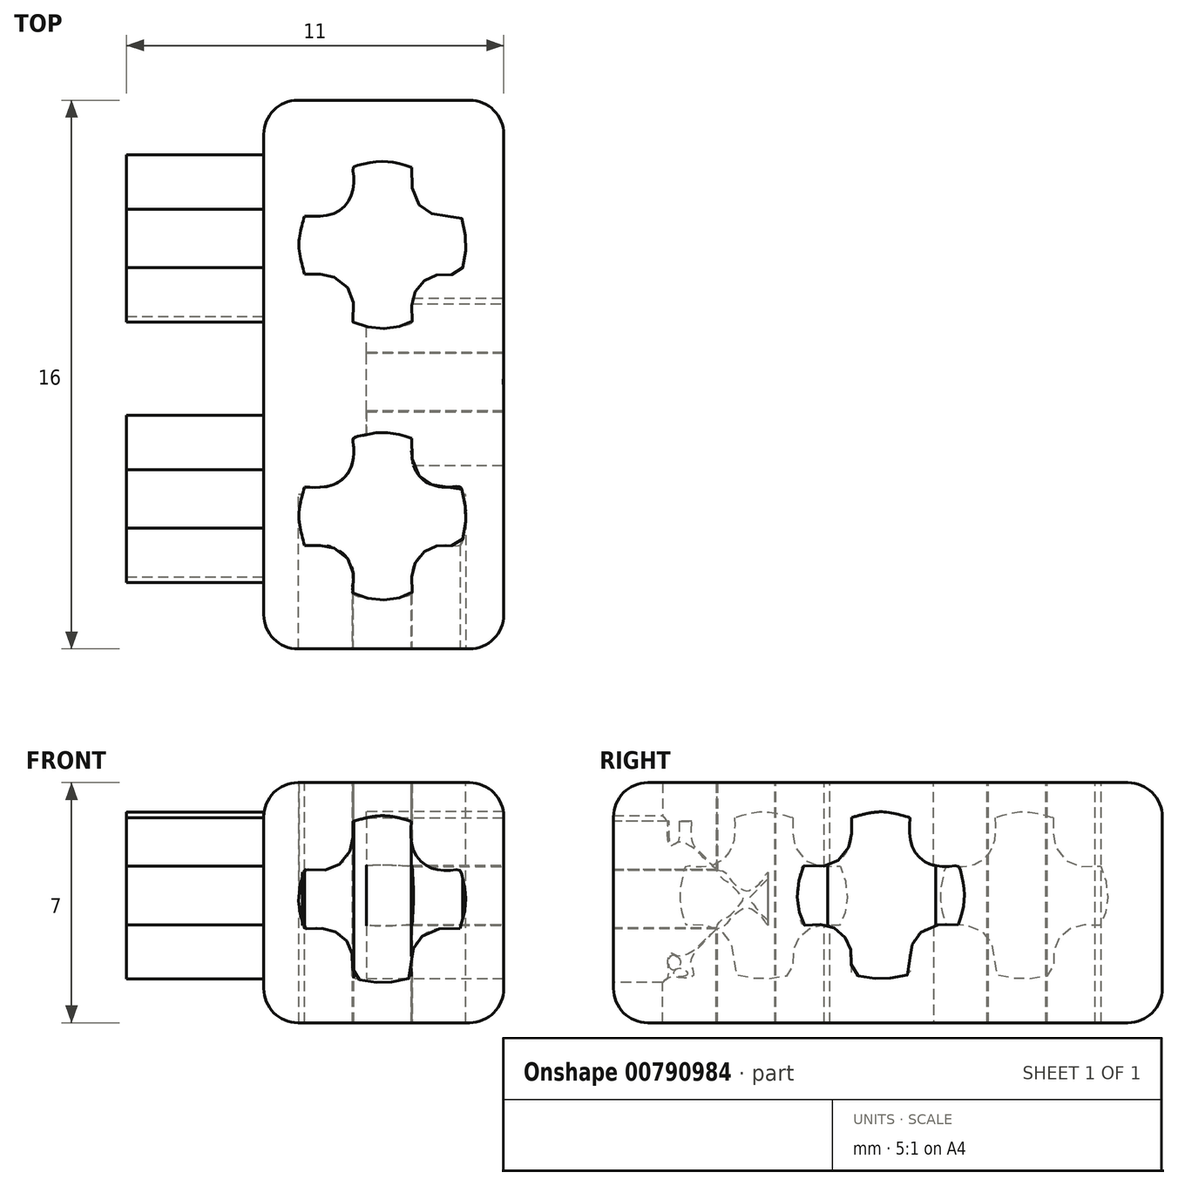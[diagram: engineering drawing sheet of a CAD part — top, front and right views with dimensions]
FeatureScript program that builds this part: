
annotation { "Feature Type Name" : "Feature", "Feature Type Description" : "" }
export const myFeature = defineFeature(function(context is Context, id is Id, definition is map)
    precondition{}
    {
        {
            var Q0;
            Q0=qCreatedBy(makeId("Top.planeOp"),FACE);
            var sketch = newSketch(context, id + "F0", { "sketchPlane" : qUnion([Q0])});
            skLineSegment(sketch, "E0.bottom", {"start": v(-3.5, 8) * mm, "end": v(3.5, 8) * mm});
            skLineSegment(sketch, "E0.top", {"start": v(-3.5, -8) * mm, "end": v(3.5, -8) * mm});
            skLineSegment(sketch, "E0.left", {"start": v(-3.5, 8) * mm, "end": v(-3.5, -8) * mm});
            skLineSegment(sketch, "E0.right", {"start": v(3.5, 8) * mm, "end": v(3.5, -8) * mm});
            skPoint(sketch, "E1", {"position": v(0, 8) * mm});
            skPoint(sketch, "E2", {"position": v(-3.5, 0) * mm});
            skSolve(sketch);
        }
        {
            var Q0;
            Q0=makeQuery(id+"F0.imprint","IMPRINT",FACE,{"disambiguationData":[TD([[makeQuery(id+"F0.imprint","IMPRINT",EDGE,{"derivedFrom":sQuery(id+"F0.wireOp",EDGE,"E0.bottom")}),-1.0]])]});
            extrude(context, id + "F1", {"entities" : qUnion([Q0]), "depth" : 7 * mm, "offsetDistance" : 25 * mm});
        }
        {
            var Q0;
            Q0=makeQuery(id+"F1.opExtrude","SWEPT_FACE",FACE,{"disambiguationData":[OSD([sQuery(id+"F0.wireOp",EDGE,"E0.left")])]});
            var sketch = newSketch(context, id + "F2", { "sketchPlane" : qUnion([Q0])});
            skFitSpline(sketch, "E3", {"points": [v(-4.82, 5.97) * mm, v(-3.94, 6.14) * mm, v(-3.12, 5.97) * mm], "startDerivative": vector(1.75, 0.5) * mm, "endDerivative": vector(1.65, -0.5) * mm});
            skFitSpline(sketch, "E4", {"points": [v(-3.12, 5.97) * mm, v(-3.12, 5.4) * mm, v(-2.97, 4.97) * mm, v(-2.66, 4.67) * mm, v(-2.31, 4.56) * mm, v(-1.9, 4.55) * mm, v(-1.7, 4.55) * mm, v(-1.62, 4.3) * mm, v(-1.54, 3.92) * mm, v(-1.53, 3.58) * mm, v(-1.58, 3.26) * mm, v(-1.7, 2.85) * mm], "startDerivative": vector(-0.26, -5.18) * mm, "endDerivative": vector(-1.41, -4.37) * mm});
            skFitSpline(sketch, "E5", {"points": [v(-4.82, 5.97) * mm, v(-4.82, 5.68) * mm, v(-4.82, 5.43) * mm, v(-4.85, 5.24) * mm, v(-5.02, 4.9) * mm, v(-5.22, 4.72) * mm, v(-5.48, 4.6) * mm, v(-5.8, 4.55) * mm, v(-6.24, 4.55) * mm, v(-6.33, 4.27) * mm, v(-6.39, 3.98) * mm, v(-6.4, 3.66) * mm, v(-6.38, 3.37) * mm, v(-6.32, 3.1) * mm, v(-6.24, 2.85) * mm, v(-6.05, 2.85) * mm, v(-5.73, 2.85) * mm, v(-5.48, 2.81) * mm, v(-5.3, 2.73) * mm, v(-5.07, 2.56) * mm, v(-4.96, 2.42) * mm, v(-4.88, 2.24) * mm, v(-4.82, 2) * mm, v(-4.82, 1.75) * mm, v(-4.82, 1.43) * mm, v(-4.56, 1.35) * mm, v(-4.21, 1.29) * mm, v(-3.94, 1.28) * mm, v(-3.67, 1.3) * mm, v(-3.3, 1.37) * mm, v(-3.12, 1.43) * mm, v(-3.12, 1.75) * mm, v(-3.11, 2.03) * mm, v(-3.01, 2.35) * mm, v(-2.88, 2.55) * mm, v(-2.61, 2.75) * mm, v(-2.2, 2.85) * mm, v(-1.7, 2.85) * mm], "startDerivative": vector(-0.02, -10.87) * mm, "endDerivative": vector(14.17, -0.52) * mm});
            skFitSpline(sketch, "E6", {"points": [v(2.78, 5.97) * mm, v(3.66, 6.14) * mm, v(4.48, 5.97) * mm], "startDerivative": vector(1.75, 0.5) * mm, "endDerivative": vector(1.65, -0.5) * mm});
            skFitSpline(sketch, "E7", {"points": [v(4.48, 5.97) * mm, v(4.48, 5.4) * mm, v(4.62, 4.97) * mm, v(4.94, 4.67) * mm, v(5.28, 4.56) * mm, v(5.7, 4.55) * mm, v(5.9, 4.55) * mm, v(5.98, 4.3) * mm, v(6.05, 3.92) * mm, v(6.06, 3.58) * mm, v(6.02, 3.26) * mm, v(5.9, 2.85) * mm], "startDerivative": vector(-0.26, -5.18) * mm, "endDerivative": vector(-1.41, -4.37) * mm});
            skFitSpline(sketch, "E8", {"points": [v(2.78, 5.97) * mm, v(2.78, 5.68) * mm, v(2.77, 5.43) * mm, v(2.75, 5.24) * mm, v(2.57, 4.9) * mm, v(2.38, 4.72) * mm, v(2.12, 4.6) * mm, v(1.8, 4.55) * mm, v(1.35, 4.55) * mm, v(1.27, 4.27) * mm, v(1.2, 3.98) * mm, v(1.19, 3.66) * mm, v(1.22, 3.37) * mm, v(1.27, 3.1) * mm, v(1.35, 2.85) * mm, v(1.55, 2.85) * mm, v(1.86, 2.85) * mm, v(2.11, 2.81) * mm, v(2.3, 2.73) * mm, v(2.52, 2.56) * mm, v(2.63, 2.42) * mm, v(2.72, 2.24) * mm, v(2.77, 2) * mm, v(2.78, 1.75) * mm, v(2.78, 1.43) * mm, v(3.03, 1.35) * mm, v(3.38, 1.29) * mm, v(3.66, 1.28) * mm, v(3.93, 1.3) * mm, v(4.3, 1.37) * mm, v(4.48, 1.43) * mm, v(4.48, 1.75) * mm, v(4.48, 2.03) * mm, v(4.58, 2.35) * mm, v(4.72, 2.55) * mm, v(4.99, 2.75) * mm, v(5.4, 2.85) * mm, v(5.9, 2.85) * mm], "startDerivative": vector(-0.02, -10.87) * mm, "endDerivative": vector(14.17, -0.52) * mm});
            skSolve(sketch);
        }
        {
            var Q0;
            Q0=makeQuery(id+"F2.imprint","IMPRINT",FACE,{"disambiguationData":[TD([[makeQuery(id+"F2.imprint","IMPRINT",EDGE,{"derivedFrom":sQuery(id+"F2.wireOp",EDGE,"E3")}),-1.0]])]});
            var Q1;
            Q1=makeQuery(id+"F2.imprint","IMPRINT",FACE,{"disambiguationData":[TD([[makeQuery(id+"F2.imprint","IMPRINT",EDGE,{"derivedFrom":sQuery(id+"F2.wireOp",EDGE,"d630b020-bbd6-4e47-9868-e03ddda9818e")}),-1.0]])]});
            var Q2;
            Q2=makeQuery(id+"F2.imprint","IMPRINT",FACE,{"disambiguationData":[TD([[makeQuery(id+"F2.imprint","IMPRINT",EDGE,{"derivedFrom":sQuery(id+"F2.wireOp",EDGE,"E6")}),-1.0]])]});
            extrude(context, id + "F3", {"entities" : qUnion([Q0, Q1, Q2]), "depth" : 4 * mm, "offsetDistance" : 25 * mm});
        }
        {
            var Q0;
            Q0=makeQuery(id+"F1.opExtrude","SWEPT_FACE",FACE,{"disambiguationData":[OSD([sQuery(id+"F0.wireOp",EDGE,"E0.top")])]});
            var sketch = newSketch(context, id + "F4", { "sketchPlane" : qUnion([Q0])});
            skFitSpline(sketch, "E9", {"points": [v(-0.9, 5.87) * mm, v(-0.02, 6.04) * mm, v(0.8, 5.87) * mm], "startDerivative": vector(1.75, 0.5) * mm, "endDerivative": vector(1.65, -0.5) * mm});
            skFitSpline(sketch, "E10", {"points": [v(0.8, 5.87) * mm, v(0.8, 5.3) * mm, v(0.95, 4.87) * mm, v(1.26, 4.57) * mm, v(1.6, 4.46) * mm, v(2.02, 4.45) * mm, v(2.22, 4.45) * mm, v(2.3, 4.2) * mm, v(2.38, 3.82) * mm, v(2.39, 3.48) * mm, v(2.34, 3.16) * mm, v(2.22, 2.75) * mm], "startDerivative": vector(-0.26, -5.18) * mm, "endDerivative": vector(-1.41, -4.37) * mm});
            skFitSpline(sketch, "E11", {"points": [v(-0.9, 5.87) * mm, v(-0.9, 5.58) * mm, v(-0.9, 5.33) * mm, v(-0.93, 5.14) * mm, v(-1.1, 4.8) * mm, v(-1.3, 4.61) * mm, v(-1.56, 4.49) * mm, v(-1.88, 4.45) * mm, v(-2.32, 4.45) * mm, v(-2.41, 4.17) * mm, v(-2.47, 3.88) * mm, v(-2.49, 3.55) * mm, v(-2.46, 3.27) * mm, v(-2.4, 3) * mm, v(-2.32, 2.75) * mm, v(-2.13, 2.75) * mm, v(-1.81, 2.75) * mm, v(-1.56, 2.71) * mm, v(-1.37, 2.63) * mm, v(-1.15, 2.46) * mm, v(-1.04, 2.32) * mm, v(-0.96, 2.14) * mm, v(-0.9, 1.9) * mm, v(-0.9, 1.65) * mm, v(-0.9, 1.33) * mm, v(-0.64, 1.25) * mm, v(-0.3, 1.19) * mm, v(-0.02, 1.18) * mm, v(0.25, 1.2) * mm, v(0.62, 1.27) * mm, v(0.8, 1.33) * mm, v(0.8, 1.65) * mm, v(0.8, 1.92) * mm, v(0.9, 2.25) * mm, v(1.04, 2.45) * mm, v(1.3, 2.65) * mm, v(1.72, 2.75) * mm, v(2.22, 2.75) * mm], "startDerivative": vector(-0.02, -10.87) * mm, "endDerivative": vector(14.17, -0.52) * mm});
            skFitSpline(sketch, "E12", {"points": [v(9.4, 6.1) * mm, v(10.29, 6.27) * mm, v(11.1, 6.1) * mm], "startDerivative": vector(1.75, 0.5) * mm, "endDerivative": vector(1.65, -0.5) * mm});
            skFitSpline(sketch, "E13", {"points": [v(11.1, 6.1) * mm, v(11.1, 5.54) * mm, v(11.25, 5.1) * mm, v(11.57, 4.8) * mm, v(11.9, 4.7) * mm, v(12.32, 4.68) * mm, v(12.52, 4.68) * mm, v(12.6, 4.44) * mm, v(12.68, 4.05) * mm, v(12.69, 3.71) * mm, v(12.65, 3.4) * mm, v(12.52, 2.98) * mm], "startDerivative": vector(-0.26, -5.18) * mm, "endDerivative": vector(-1.41, -4.37) * mm});
            skFitSpline(sketch, "E14", {"points": [v(9.4, 6.1) * mm, v(9.4, 5.8) * mm, v(9.4, 5.56) * mm, v(9.37, 5.37) * mm, v(9.2, 5.03) * mm, v(9, 4.85) * mm, v(8.74, 4.72) * mm, v(8.42, 4.68) * mm, v(7.98, 4.68) * mm, v(7.9, 4.4) * mm, v(7.83, 4.12) * mm, v(7.81, 3.79) * mm, v(7.84, 3.5) * mm, v(7.9, 3.23) * mm, v(7.98, 2.98) * mm, v(8.18, 2.98) * mm, v(8.5, 2.98) * mm, v(8.74, 2.95) * mm, v(8.93, 2.87) * mm, v(9.15, 2.7) * mm, v(9.26, 2.55) * mm, v(9.35, 2.37) * mm, v(9.4, 2.13) * mm, v(9.4, 1.88) * mm, v(9.4, 1.56) * mm, v(9.66, 1.48) * mm, v(10, 1.42) * mm, v(10.29, 1.4) * mm, v(10.55, 1.43) * mm, v(10.92, 1.5) * mm, v(11.1, 1.56) * mm, v(11.1, 1.88) * mm, v(11.1, 2.16) * mm, v(11.2, 2.49) * mm, v(11.34, 2.68) * mm, v(11.61, 2.88) * mm, v(12.03, 2.98) * mm, v(12.52, 2.98) * mm], "startDerivative": vector(-0.02, -10.87) * mm, "endDerivative": vector(14.17, -0.52) * mm});
            skFitSpline(sketch, "E15", {"points": [v(18.93, 6.02) * mm, v(19.82, 6.2) * mm, v(20.63, 6.02) * mm], "startDerivative": vector(1.75, 0.5) * mm, "endDerivative": vector(1.65, -0.5) * mm});
            skFitSpline(sketch, "E16", {"points": [v(20.63, 6.02) * mm, v(20.64, 5.46) * mm, v(20.78, 5.03) * mm, v(21.1, 4.73) * mm, v(21.44, 4.61) * mm, v(21.85, 4.6) * mm, v(22.05, 4.6) * mm, v(22.13, 4.36) * mm, v(22.2, 3.98) * mm, v(22.22, 3.64) * mm, v(22.18, 3.32) * mm, v(22.05, 2.9) * mm], "startDerivative": vector(-0.26, -5.18) * mm, "endDerivative": vector(-1.41, -4.37) * mm});
            skFitSpline(sketch, "E17", {"points": [v(18.93, 6.02) * mm, v(18.93, 5.73) * mm, v(18.93, 5.48) * mm, v(18.9, 5.3) * mm, v(18.73, 4.95) * mm, v(18.53, 4.77) * mm, v(18.27, 4.64) * mm, v(17.95, 4.6) * mm, v(17.51, 4.6) * mm, v(17.42, 4.32) * mm, v(17.37, 4.04) * mm, v(17.35, 3.7) * mm, v(17.37, 3.42) * mm, v(17.43, 3.15) * mm, v(17.51, 2.9) * mm, v(17.7, 2.9) * mm, v(18.02, 2.9) * mm, v(18.27, 2.87) * mm, v(18.46, 2.79) * mm, v(18.68, 2.61) * mm, v(18.79, 2.47) * mm, v(18.88, 2.3) * mm, v(18.93, 2.05) * mm, v(18.93, 1.8) * mm, v(18.93, 1.48) * mm, v(19.2, 1.4) * mm, v(19.54, 1.34) * mm, v(19.82, 1.33) * mm, v(20.08, 1.35) * mm, v(20.45, 1.42) * mm, v(20.63, 1.48) * mm, v(20.63, 1.8) * mm, v(20.64, 2.08) * mm, v(20.74, 2.4) * mm, v(20.88, 2.6) * mm, v(21.14, 2.8) * mm, v(21.56, 2.9) * mm, v(22.05, 2.9) * mm], "startDerivative": vector(-0.02, -10.87) * mm, "endDerivative": vector(14.17, -0.52) * mm});
            skSolve(sketch);
        }
        {
            var Q0;
            Q0=makeQuery(id+"F4.imprint","IMPRINT",FACE,{"disambiguationData":[TD([[makeQuery(id+"F4.imprint","IMPRINT",EDGE,{"derivedFrom":sQuery(id+"F4.wireOp",EDGE,"E9")}),-1.0]])]});
            extrude(context, id + "F5", {"entities" : qUnion([Q0]), "operationType" : NewBodyOperationType.REMOVE, "oppositeDirection" : true, "depth" : 4.5 * mm, "offsetDistance" : 25 * mm});
        }
        {
            var Q0;
            Q0=makeQuery(id+"F1.opExtrude","SWEPT_FACE",FACE,{"disambiguationData":[OSD([sQuery(id+"F0.wireOp",EDGE,"E0.right")])]});
            var sketch = newSketch(context, id + "F6", { "sketchPlane" : qUnion([Q0])});
            skFitSpline(sketch, "E18", {"points": [v(-1.06, 5.98) * mm, v(-0.18, 6.15) * mm, v(0.64, 5.98) * mm], "startDerivative": vector(1.75, 0.5) * mm, "endDerivative": vector(1.65, -0.5) * mm});
            skFitSpline(sketch, "E19", {"points": [v(0.64, 5.98) * mm, v(0.64, 5.42) * mm, v(0.79, 4.98) * mm, v(1.1, 4.68) * mm, v(1.44, 4.57) * mm, v(1.86, 4.56) * mm, v(2.06, 4.56) * mm, v(2.14, 4.32) * mm, v(2.21, 3.93) * mm, v(2.22, 3.6) * mm, v(2.18, 3.27) * mm, v(2.06, 2.86) * mm], "startDerivative": vector(-0.26, -5.18) * mm, "endDerivative": vector(-1.41, -4.37) * mm});
            skFitSpline(sketch, "E20", {"points": [v(-1.06, 5.98) * mm, v(-1.06, 5.69) * mm, v(-1.06, 5.44) * mm, v(-1.1, 5.25) * mm, v(-1.26, 4.9) * mm, v(-1.46, 4.73) * mm, v(-1.72, 4.6) * mm, v(-2.04, 4.56) * mm, v(-2.48, 4.56) * mm, v(-2.57, 4.28) * mm, v(-2.63, 4) * mm, v(-2.65, 3.67) * mm, v(-2.62, 3.38) * mm, v(-2.56, 3.11) * mm, v(-2.48, 2.86) * mm, v(-2.29, 2.86) * mm, v(-1.97, 2.86) * mm, v(-1.73, 2.82) * mm, v(-1.54, 2.74) * mm, v(-1.31, 2.57) * mm, v(-1.2, 2.43) * mm, v(-1.12, 2.25) * mm, v(-1.06, 2) * mm, v(-1.06, 1.76) * mm, v(-1.06, 1.44) * mm, v(-0.8, 1.36) * mm, v(-0.46, 1.3) * mm, v(-0.18, 1.29) * mm, v(0.09, 1.3) * mm, v(0.45, 1.38) * mm, v(0.64, 1.44) * mm, v(0.64, 1.76) * mm, v(0.64, 2.04) * mm, v(0.74, 2.36) * mm, v(0.88, 2.56) * mm, v(1.15, 2.76) * mm, v(1.56, 2.86) * mm, v(2.06, 2.86) * mm], "startDerivative": vector(-0.02, -10.87) * mm, "endDerivative": vector(14.17, -0.52) * mm});
            skSolve(sketch);
        }
        {
            var Q0;
            Q0=makeQuery(id+"F6.imprint","IMPRINT",FACE,{"disambiguationData":[TD([[makeQuery(id+"F6.imprint","IMPRINT",EDGE,{"derivedFrom":sQuery(id+"F6.wireOp",EDGE,"E18")}),-1.0]])]});
            extrude(context, id + "F7", {"entities" : qUnion([Q0]), "operationType" : NewBodyOperationType.REMOVE, "oppositeDirection" : true, "depth" : 4 * mm, "offsetDistance" : 25 * mm});
        }
        {
            var Q0;
            Q0=makeQuery(id+"F1.opExtrude","CAP_FACE",FACE,{"disambiguationData":[OSD([sQuery(id+"F0.wireOp",EDGE,"E0.bottom"),sQuery(id+"F0.wireOp",EDGE,"E0.top"),sQuery(id+"F0.wireOp",EDGE,"E0.left"),sQuery(id+"F0.wireOp",EDGE,"E0.right")])],"isStart":false});
            var sketch = newSketch(context, id + "F8", { "sketchPlane" : qUnion([Q0])});
            skFitSpline(sketch, "E21", {"points": [v(-2.3, -4.98) * mm, v(-2.47, -4.1) * mm, v(-2.3, -3.28) * mm], "startDerivative": vector(-0.5, 1.75) * mm, "endDerivative": vector(0.5, 1.65) * mm});
            skFitSpline(sketch, "E22", {"points": [v(-2.3, -3.28) * mm, v(-1.74, -3.28) * mm, v(-1.3, -3.13) * mm, v(-1, -2.82) * mm, v(-0.9, -2.48) * mm, v(-0.89, -2.06) * mm, v(-0.89, -1.86) * mm, v(-0.64, -1.78) * mm, v(-0.26, -1.7) * mm, v(0.08, -1.7) * mm, v(0.4, -1.74) * mm, v(0.81, -1.86) * mm], "startDerivative": vector(5.18, -0.26) * mm, "endDerivative": vector(4.37, -1.41) * mm});
            skFitSpline(sketch, "E23", {"points": [v(-2.3, -4.98) * mm, v(-2.01, -4.98) * mm, v(-1.76, -4.98) * mm, v(-1.57, -5.01) * mm, v(-1.23, -5.18) * mm, v(-1.05, -5.38) * mm, v(-0.92, -5.64) * mm, v(-0.89, -5.96) * mm, v(-0.89, -6.4) * mm, v(-0.6, -6.5) * mm, v(-0.32, -6.55) * mm, v(0.01, -6.57) * mm, v(0.3, -6.54) * mm, v(0.56, -6.48) * mm, v(0.81, -6.4) * mm, v(0.81, -6.2) * mm, v(0.82, -5.9) * mm, v(0.85, -5.65) * mm, v(0.93, -5.46) * mm, v(1.1, -5.23) * mm, v(1.24, -5.12) * mm, v(1.42, -5.04) * mm, v(1.67, -4.98) * mm, v(1.92, -4.98) * mm, v(2.24, -4.98) * mm, v(2.32, -4.72) * mm, v(2.38, -4.38) * mm, v(2.39, -4.1) * mm, v(2.37, -3.83) * mm, v(2.3, -3.47) * mm, v(2.24, -3.28) * mm, v(1.92, -3.28) * mm, v(1.64, -3.28) * mm, v(1.31, -3.18) * mm, v(1.12, -3.04) * mm, v(0.91, -2.77) * mm, v(0.81, -2.36) * mm, v(0.81, -1.86) * mm], "startDerivative": vector(10.87, -0.02) * mm, "endDerivative": vector(0.52, 14.17) * mm});
            skFitSpline(sketch, "E24", {"points": [v(-2.3, 2.92) * mm, v(-2.47, 3.8) * mm, v(-2.3, 4.62) * mm], "startDerivative": vector(-0.5, 1.75) * mm, "endDerivative": vector(0.5, 1.65) * mm});
            skFitSpline(sketch, "E25", {"points": [v(-2.3, 4.62) * mm, v(-1.74, 4.62) * mm, v(-1.3, 4.77) * mm, v(-1, 5.08) * mm, v(-0.9, 5.43) * mm, v(-0.89, 5.84) * mm, v(-0.89, 6.04) * mm, v(-0.64, 6.12) * mm, v(-0.26, 6.2) * mm, v(0.08, 6.2) * mm, v(0.4, 6.16) * mm, v(0.81, 6.04) * mm], "startDerivative": vector(5.18, -0.26) * mm, "endDerivative": vector(4.37, -1.41) * mm});
            skFitSpline(sketch, "E26", {"points": [v(-2.3, 2.92) * mm, v(-2.01, 2.92) * mm, v(-1.76, 2.92) * mm, v(-1.57, 2.9) * mm, v(-1.23, 2.72) * mm, v(-1.05, 2.52) * mm, v(-0.92, 2.26) * mm, v(-0.89, 1.94) * mm, v(-0.89, 1.5) * mm, v(-0.6, 1.41) * mm, v(-0.32, 1.35) * mm, v(0.01, 1.33) * mm, v(0.3, 1.36) * mm, v(0.56, 1.42) * mm, v(0.81, 1.5) * mm, v(0.81, 1.7) * mm, v(0.82, 2) * mm, v(0.85, 2.26) * mm, v(0.93, 2.45) * mm, v(1.1, 2.67) * mm, v(1.24, 2.78) * mm, v(1.42, 2.87) * mm, v(1.67, 2.92) * mm, v(1.92, 2.92) * mm, v(2.24, 2.92) * mm, v(2.32, 3.18) * mm, v(2.38, 3.53) * mm, v(2.39, 3.8) * mm, v(2.37, 4.07) * mm, v(2.3, 4.44) * mm, v(2.24, 4.62) * mm, v(1.92, 4.62) * mm, v(1.64, 4.63) * mm, v(1.31, 4.73) * mm, v(1.12, 4.86) * mm, v(0.91, 5.13) * mm, v(0.81, 5.55) * mm, v(0.81, 6.04) * mm], "startDerivative": vector(10.87, -0.02) * mm, "endDerivative": vector(0.52, 14.17) * mm});
            skSolve(sketch);
        }
        {
            var Q0;
            Q0=makeQuery(id+"F8.imprint","IMPRINT",FACE,{"disambiguationData":[TD([[makeQuery(id+"F8.imprint","IMPRINT",EDGE,{"derivedFrom":sQuery(id+"F8.wireOp",EDGE,"E21")}),-1.0]])]});
            var Q1;
            Q1=makeQuery(id+"F8.imprint","IMPRINT",FACE,{"disambiguationData":[TD([[makeQuery(id+"F8.imprint","IMPRINT",EDGE,{"derivedFrom":sQuery(id+"F8.wireOp",EDGE,"E24")}),-1.0]])]});
            extrude(context, id + "F9", {"entities" : qUnion([Q0, Q1]), "operationType" : NewBodyOperationType.REMOVE, "oppositeDirection" : true, "depth" : 9.6 * mm, "offsetDistance" : 25 * mm});
        }
        {
            var Q0;
            Q0=makeQuery(id+"F1.opExtrude","CAP_EDGE",EDGE,{"disambiguationData":[OSD([sQuery(id+"F0.wireOp",EDGE,"E0.bottom")])],"isStart":false});
            var Q1;
            Q1=makeQuery(id+"F1.opExtrude","SWEPT_EDGE",EDGE,{"disambiguationData":[OSD([sQuery(id+"F0.wireOp",EDGE,"E0.bottom"),sQuery(id+"F0.wireOp",EDGE,"E0.left")])]});
            var Q2;
            Q2=makeQuery(id+"F1.opExtrude","CAP_EDGE",EDGE,{"disambiguationData":[OSD([sQuery(id+"F0.wireOp",EDGE,"E0.bottom")])],"isStart":true});
            var Q3;
            Q3=makeQuery(id+"F1.opExtrude","SWEPT_EDGE",EDGE,{"disambiguationData":[OSD([sQuery(id+"F0.wireOp",EDGE,"E0.bottom"),sQuery(id+"F0.wireOp",EDGE,"E0.right")])]});
            var Q4;
            Q4=makeQuery(id+"F1.opExtrude","CAP_EDGE",EDGE,{"disambiguationData":[OSD([sQuery(id+"F0.wireOp",EDGE,"E0.top")])],"isStart":false});
            var Q5;
            Q5=makeQuery(id+"F1.opExtrude","SWEPT_EDGE",EDGE,{"disambiguationData":[OSD([sQuery(id+"F0.wireOp",EDGE,"E0.top"),sQuery(id+"F0.wireOp",EDGE,"E0.left")])]});
            var Q6;
            Q6=makeQuery(id+"F1.opExtrude","CAP_EDGE",EDGE,{"disambiguationData":[OSD([sQuery(id+"F0.wireOp",EDGE,"E0.top")])],"isStart":true});
            var Q7;
            Q7=makeQuery(id+"F1.opExtrude","SWEPT_EDGE",EDGE,{"disambiguationData":[OSD([sQuery(id+"F0.wireOp",EDGE,"E0.top"),sQuery(id+"F0.wireOp",EDGE,"E0.right")])]});
            fillet(context, id + "F10", {"entities" : qUnion([Q0, Q1, Q2, Q3, Q4, Q5, Q6, Q7]), "radius" : 1 * mm, "tangentPropagation" : true, "allowEdgeOverflow" : false});
        }
        {
            var Q0;
            Q0=makeQuery(id+"F1.opExtrude","CAP_EDGE",EDGE,{"disambiguationData":[OSD([sQuery(id+"F0.wireOp",EDGE,"E0.left")])],"isStart":false});
            var Q1;
            {var subQ0=sQuery(id+"F0.wireOp",EDGE,"E0.bottom");Q1=makeQuery(id+"F10.opFillet","BLEND_EDGE",EDGE,{"blendedFrom":[makeQuery(id+"F1.opExtrude","SWEPT_EDGE",EDGE,{"disambiguationData":[OSD([subQ0,sQuery(id+"F0.wireOp",EDGE,"E0.right")])]}),makeQuery(id+"F1.opExtrude","CAP_EDGE",EDGE,{"disambiguationData":[OSD([subQ0])],"isStart":false})],"blendedInto":[]});}
            var Q2;
            Q2=makeQuery(id+"F1.opExtrude","CAP_EDGE",EDGE,{"disambiguationData":[OSD([sQuery(id+"F0.wireOp",EDGE,"E0.right")])],"isStart":false});
            var Q3;
            {var subQ0=sQuery(id+"F0.wireOp",EDGE,"E0.top");Q3=makeQuery(id+"F10.opFillet","BLEND_EDGE",EDGE,{"blendedFrom":[makeQuery(id+"F1.opExtrude","SWEPT_EDGE",EDGE,{"disambiguationData":[OSD([subQ0,sQuery(id+"F0.wireOp",EDGE,"E0.left")])]}),makeQuery(id+"F1.opExtrude","CAP_EDGE",EDGE,{"disambiguationData":[OSD([subQ0])],"isStart":false})],"blendedInto":[]});}
            var Q4;
            {var subQ0=sQuery(id+"F0.wireOp",EDGE,"E0.top");Q4=makeQuery(id+"F10.opFillet","BLEND_EDGE",EDGE,{"blendedFrom":[makeQuery(id+"F1.opExtrude","SWEPT_EDGE",EDGE,{"disambiguationData":[OSD([subQ0,sQuery(id+"F0.wireOp",EDGE,"E0.right")])]}),makeQuery(id+"F1.opExtrude","CAP_EDGE",EDGE,{"disambiguationData":[OSD([subQ0])],"isStart":false})],"blendedInto":[]});}
            var Q5;
            {var subQ0=sQuery(id+"F0.wireOp",EDGE,"E0.bottom");Q5=makeQuery(id+"F10.opFillet","BLEND_EDGE",EDGE,{"blendedFrom":[makeQuery(id+"F1.opExtrude","SWEPT_EDGE",EDGE,{"disambiguationData":[OSD([subQ0,sQuery(id+"F0.wireOp",EDGE,"E0.left")])]}),makeQuery(id+"F1.opExtrude","CAP_EDGE",EDGE,{"disambiguationData":[OSD([subQ0])],"isStart":true})],"blendedInto":[]});}
            var Q6;
            Q6=makeQuery(id+"F1.opExtrude","CAP_EDGE",EDGE,{"disambiguationData":[OSD([sQuery(id+"F0.wireOp",EDGE,"E0.left")])],"isStart":true});
            var Q7;
            {var subQ0=sQuery(id+"F0.wireOp",EDGE,"E0.top");Q7=makeQuery(id+"F10.opFillet","BLEND_EDGE",EDGE,{"blendedFrom":[makeQuery(id+"F1.opExtrude","SWEPT_EDGE",EDGE,{"disambiguationData":[OSD([subQ0,sQuery(id+"F0.wireOp",EDGE,"E0.left")])]}),makeQuery(id+"F1.opExtrude","CAP_EDGE",EDGE,{"disambiguationData":[OSD([subQ0])],"isStart":true})],"blendedInto":[]});}
            var Q8;
            {var subQ0=sQuery(id+"F0.wireOp",EDGE,"E0.bottom");Q8=makeQuery(id+"F10.opFillet","BLEND_EDGE",EDGE,{"blendedFrom":[makeQuery(id+"F1.opExtrude","SWEPT_EDGE",EDGE,{"disambiguationData":[OSD([subQ0,sQuery(id+"F0.wireOp",EDGE,"E0.right")])]}),makeQuery(id+"F1.opExtrude","CAP_EDGE",EDGE,{"disambiguationData":[OSD([subQ0])],"isStart":true})],"blendedInto":[]});}
            var Q9;
            Q9=makeQuery(id+"F1.opExtrude","CAP_EDGE",EDGE,{"disambiguationData":[OSD([sQuery(id+"F0.wireOp",EDGE,"E0.right")])],"isStart":true});
            var Q10;
            {var subQ0=sQuery(id+"F0.wireOp",EDGE,"E0.top");Q10=makeQuery(id+"F10.opFillet","BLEND_EDGE",EDGE,{"blendedFrom":[makeQuery(id+"F1.opExtrude","SWEPT_EDGE",EDGE,{"disambiguationData":[OSD([subQ0,sQuery(id+"F0.wireOp",EDGE,"E0.right")])]}),makeQuery(id+"F1.opExtrude","CAP_EDGE",EDGE,{"disambiguationData":[OSD([subQ0])],"isStart":true})],"blendedInto":[]});}
            fillet(context, id + "F11", {"entities" : qUnion([Q0, Q1, Q2, Q3, Q4, Q5, Q6, Q7, Q8, Q9, Q10]), "radius" : 1 * mm, "tangentPropagation" : true, "allowEdgeOverflow" : false});
        }
    });
